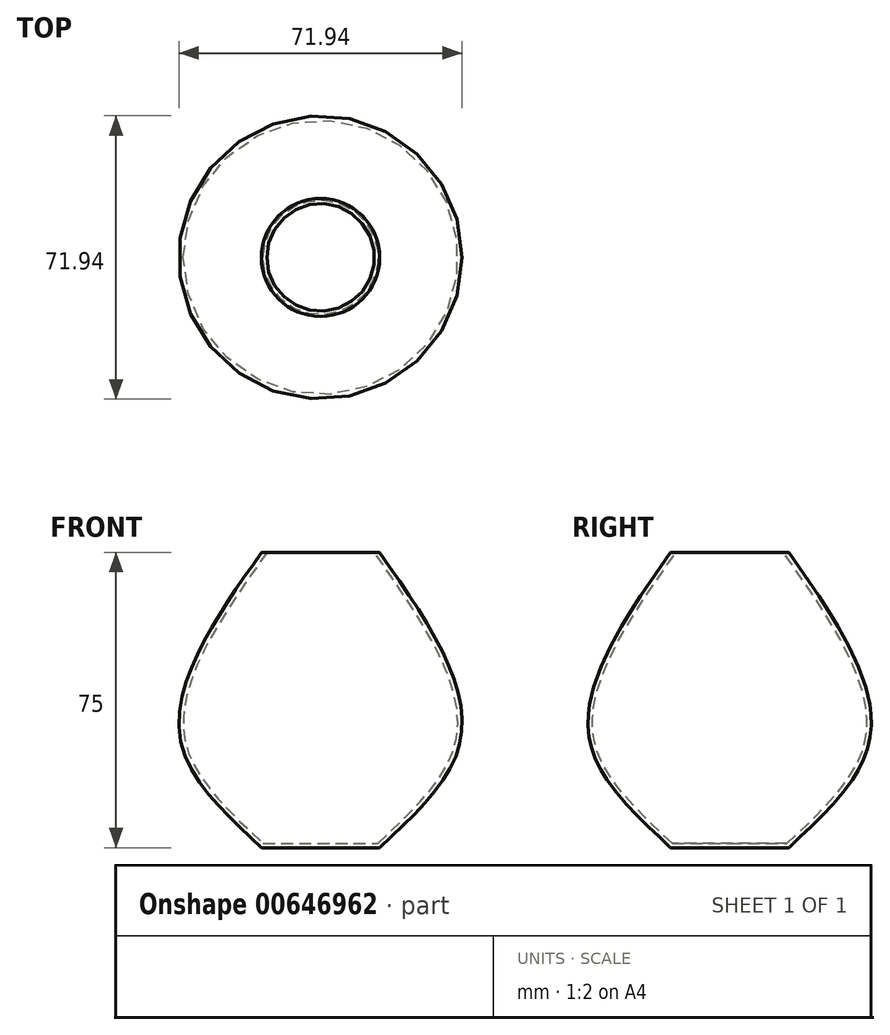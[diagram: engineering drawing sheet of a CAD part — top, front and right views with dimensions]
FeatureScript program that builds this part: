
annotation { "Feature Type Name" : "Feature", "Feature Type Description" : "" }
export const myFeature = defineFeature(function(context is Context, id is Id, definition is map)
    precondition{}
    {
        {
            var Q0;
            Q0=qCreatedBy(makeId("Top.planeOp"),FACE);
            var sketch = newSketch(context, id + "F0", { "sketchPlane" : qUnion([Q0])});
            skCircle(sketch, "E0", {"center": v(0, 0) * mm, "radius": 35 * mm});
            skSolve(sketch);
        }
        {
            var Q0;
            Q0=qCreatedBy(makeId("Top.planeOp"),FACE);
            cPlane(context, id + "F1", {"entities" : qUnion([Q0]), "cplaneType" : CPlaneType.OFFSET, "offset" : 50 * mm, "width" : 150 * mm, "height" : 150 * mm});
        }
        {
            var Q0;
            Q0=qCreatedBy(id+"F1.planeOp",FACE);
            var sketch = newSketch(context, id + "F2", { "sketchPlane" : qUnion([Q0])});
            skCircle(sketch, "E1", {"center": v(0, 0) * mm, "radius": 15 * mm});
            skSolve(sketch);
        }
        {
            var Q0;
            Q0=qCreatedBy(makeId("Top.planeOp"),FACE);
            cPlane(context, id + "F3", {"entities" : qUnion([Q0]), "cplaneType" : CPlaneType.OFFSET, "offset" : 25 * mm, "oppositeDirection" : true, "width" : 150 * mm, "height" : 150 * mm});
        }
        {
            var Q0;
            Q0=qCreatedBy(id+"F3.planeOp",FACE);
            var sketch = newSketch(context, id + "F4", { "sketchPlane" : qUnion([Q0])});
            skCircle(sketch, "E2", {"center": v(0, 0) * mm, "radius": 15 * mm});
            skSolve(sketch);
        }
        {
            var Q0;
            Q0=makeQuery(id+"F2.imprint","IMPRINT",FACE,{"disambiguationData":[TD([[makeQuery(id+"F2.imprint","IMPRINT",EDGE,{"derivedFrom":sQuery(id+"F2.wireOp",EDGE,"E1")}),1.0]])]});
            var Q1;
            Q1=makeQuery(id+"F0.imprint","IMPRINT",FACE,{"disambiguationData":[TD([[makeQuery(id+"F0.imprint","IMPRINT",EDGE,{"derivedFrom":sQuery(id+"F0.wireOp",EDGE,"E0")}),1.0]])]});
            var Q2;
            Q2=makeQuery(id+"F4.imprint","IMPRINT",FACE,{"disambiguationData":[TD([[makeQuery(id+"F4.imprint","IMPRINT",EDGE,{"derivedFrom":sQuery(id+"F4.wireOp",EDGE,"E2")}),1.0]])]});
            loft(context, id + "F5", {"sheetProfilesArray" : [{ "sheetProfileEntities" : qUnion([Q0]) }, { "sheetProfileEntities" : qUnion([Q1]) }, { "sheetProfileEntities" : qUnion([Q2]) }]});
        }
        {
            var Q0;
            Q0=makeQuery(id+"F5.opLoft","CAP_FACE",FACE,{"disambiguationData":[OSD([makeQuery(id+"F2.imprint","IMPRINT",FACE,{"disambiguationData":[TD([[makeQuery(id+"F2.imprint","IMPRINT",EDGE,{"derivedFrom":sQuery(id+"F2.wireOp",EDGE,"E1")}),1.0]])]})])],"isStart":true});
            shell(context, id + "F6", {"entities" : qUnion([Q0]), "thickness" : 1.1 * mm});
        }
    });
